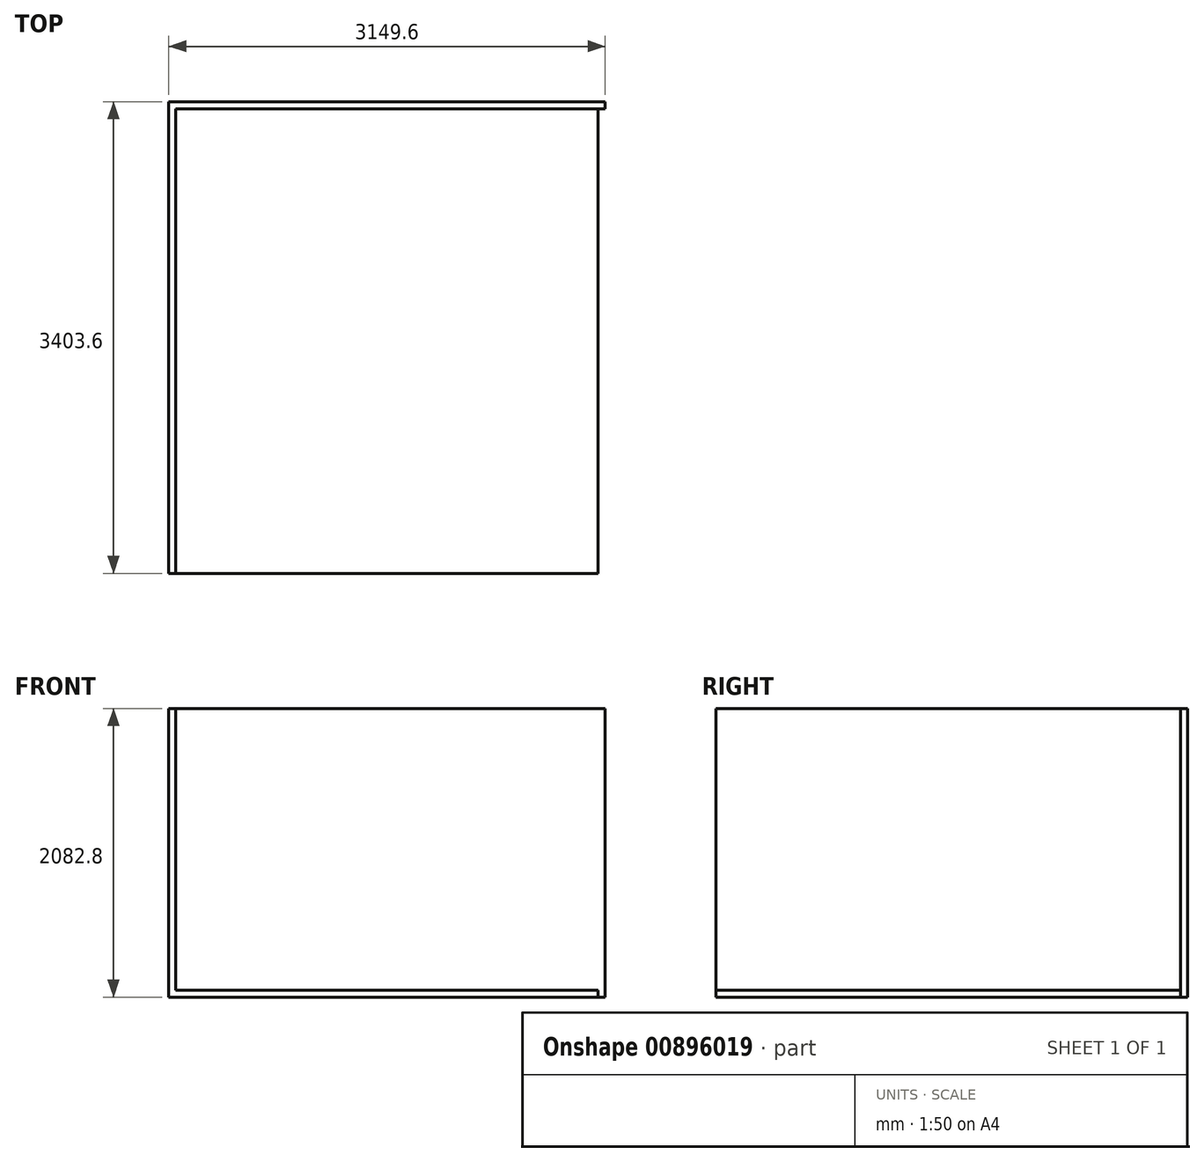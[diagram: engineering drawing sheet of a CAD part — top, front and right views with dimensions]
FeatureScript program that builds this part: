
annotation { "Feature Type Name" : "Feature", "Feature Type Description" : "" }
export const myFeature = defineFeature(function(context is Context, id is Id, definition is map)
    precondition{}
    {
        {
            var Q0;
            Q0=qCreatedBy(makeId("Top.planeOp"),FACE);
            var sketch = newSketch(context, id + "F0", { "sketchPlane" : qUnion([Q0])});
            skLineSegment(sketch, "E0.bottom", {"start": v(0, 0) * mm, "end": v(3048, 0) * mm});
            skLineSegment(sketch, "E0.top", {"start": v(0, 3352.8) * mm, "end": v(3048, 3352.8) * mm});
            skLineSegment(sketch, "E0.left", {"start": v(0, 0) * mm, "end": v(0, 3352.8) * mm});
            skLineSegment(sketch, "E0.right", {"start": v(3048, 0) * mm, "end": v(3048, 3352.8) * mm});
            skSolve(sketch);
        }
        {
            var Q0;
            Q0=makeQuery(id+"F0.imprint","IMPRINT",FACE,{"disambiguationData":[TD([[makeQuery(id+"F0.imprint","IMPRINT",EDGE,{"derivedFrom":sQuery(id+"F0.wireOp",EDGE,"E0.bottom")}),1.0]])]});
            extrude(context, id + "F1", {"entities" : qUnion([Q0]), "depth" : 50.8 * mm, "offsetDistance" : 25.4 * mm});
        }
        {
            var Q0;
            Q0=makeQuery(id+"F1.opExtrude","CAP_FACE",FACE,{"disambiguationData":[OSD([sQuery(id+"F0.wireOp",EDGE,"E0.bottom"),sQuery(id+"F0.wireOp",EDGE,"E0.top"),sQuery(id+"F0.wireOp",EDGE,"E0.left"),sQuery(id+"F0.wireOp",EDGE,"E0.right")])],"isStart":true});
            var sketch = newSketch(context, id + "F2", { "sketchPlane" : qUnion([Q0])});
            skLineSegment(sketch, "E1.bottom", {"start": v(0, 0) * mm, "end": v(-50.8, 0) * mm});
            skLineSegment(sketch, "E1.top", {"start": v(0, -3352.8) * mm, "end": v(-50.8, -3352.8) * mm});
            skLineSegment(sketch, "E1.left", {"start": v(0, 0) * mm, "end": v(0, -3352.8) * mm});
            skLineSegment(sketch, "E1.right", {"start": v(-50.8, 0) * mm, "end": v(-50.8, -3352.8) * mm});
            skLineSegment(sketch, "E2.bottom", {"start": v(-50.8, -3352.8) * mm, "end": v(3098.8, -3352.8) * mm});
            skLineSegment(sketch, "E2.top", {"start": v(-50.8, -3403.6) * mm, "end": v(3098.8, -3403.6) * mm});
            skLineSegment(sketch, "E2.left", {"start": v(-50.8, -3352.8) * mm, "end": v(-50.8, -3403.6) * mm});
            skLineSegment(sketch, "E2.right", {"start": v(3098.8, -3352.8) * mm, "end": v(3098.8, -3403.6) * mm});
            skLineSegment(sketch, "E3.bottom", {"start": v(3098.8, -3352.8) * mm, "end": v(3048, -3352.8) * mm});
            skLineSegment(sketch, "E3.top", {"start": v(3098.8, 0) * mm, "end": v(3048, 0) * mm});
            skLineSegment(sketch, "E3.left", {"start": v(3098.8, -3352.8) * mm, "end": v(3098.8, 0) * mm});
            skLineSegment(sketch, "E3.right", {"start": v(3048, -3352.8) * mm, "end": v(3048, 0) * mm});
            skSolve(sketch);
        }
        {
            var Q0;
            Q0=makeQuery(id+"F2.imprint","IMPRINT",FACE,{"disambiguationData":[TD([[makeQuery(id+"F2.imprint","IMPRINT",EDGE,{"derivedFrom":sQuery(id+"F2.wireOp",EDGE,"E1.bottom")}),1.0]])]});
            var Q1;
            Q1=makeQuery(id+"F2.imprint","IMPRINT",FACE,{"disambiguationData":[TD([[makeQuery(id+"F2.imprint","IMPRINT",EDGE,{"derivedFrom":sQuery(id+"F2.wireOp",EDGE,"E2.top")}),1.0]])]});
            var Q2;
            Q2=makeQuery(id+"F2.imprint","IMPRINT",FACE,{"disambiguationData":[TD([[makeQuery(id+"F2.imprint","IMPRINT",EDGE,{"derivedFrom":sQuery(id+"F2.wireOp",EDGE,"E3.bottom")}),-1.0]])]});
            var Q3;
            Q3=makeQuery(id+"F1.opExtrude","CAP_FACE",FACE,{"disambiguationData":[OSD([sQuery(id+"F0.wireOp",EDGE,"E0.bottom"),sQuery(id+"F0.wireOp",EDGE,"E0.top"),sQuery(id+"F0.wireOp",EDGE,"E0.left"),sQuery(id+"F0.wireOp",EDGE,"E0.right")])],"isStart":false});
            extrude(context, id + "F3", {"entities" : qUnion([Q0, Q1, Q2]), "operationType" : NewBodyOperationType.ADD, "endBound" : BoundingType.UP_TO_SURFACE, "oppositeDirection" : true, "depth" : 25.4 * mm, "endBoundEntityFace" : qUnion([Q3]), "hasOffset" : true, "offsetDistance" : 2032 * mm, "offsetOppositeDirection" : true});
        }
    });
